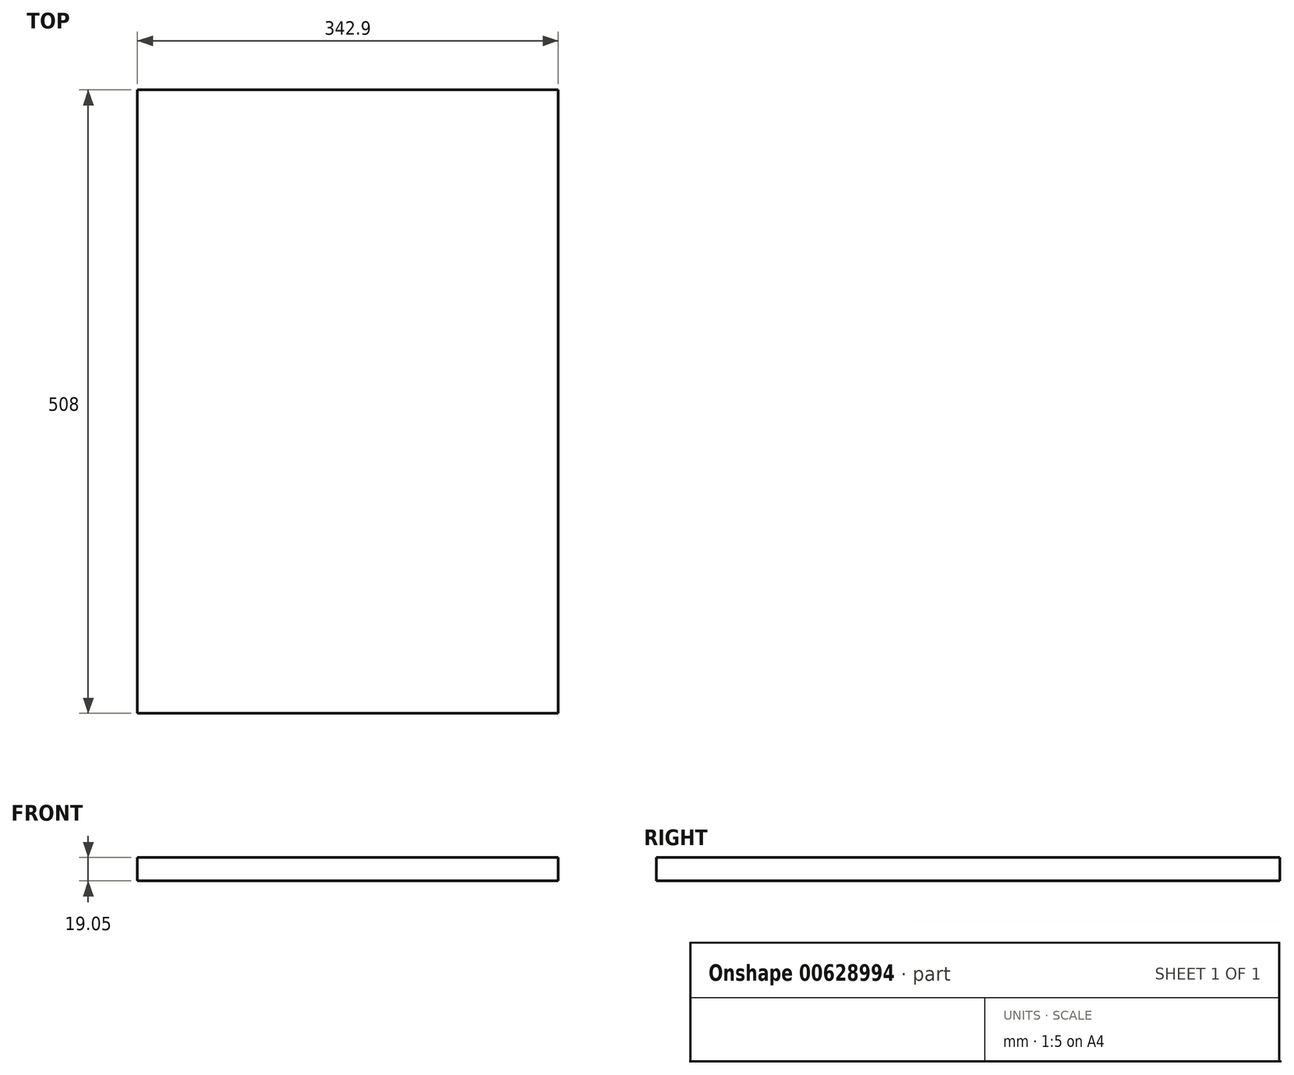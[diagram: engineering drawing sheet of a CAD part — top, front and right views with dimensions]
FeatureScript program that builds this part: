
annotation { "Feature Type Name" : "Feature", "Feature Type Description" : "" }
export const myFeature = defineFeature(function(context is Context, id is Id, definition is map)
    precondition{}
    {
        {
            var Q0;
            Q0=qCreatedBy(makeId("Top.planeOp"),FACE);
            var sketch = newSketch(context, id + "F0", { "sketchPlane" : qUnion([Q0])});
            skLineSegment(sketch, "E0.bottom", {"start": v(-171.45, 254) * mm, "end": v(171.45, 254) * mm});
            skLineSegment(sketch, "E0.top", {"start": v(-171.45, -254) * mm, "end": v(171.45, -254) * mm});
            skLineSegment(sketch, "E0.left", {"start": v(-171.45, 254) * mm, "end": v(-171.45, -254) * mm});
            skLineSegment(sketch, "E0.right", {"start": v(171.45, 254) * mm, "end": v(171.45, -254) * mm});
            skPoint(sketch, "E0.middle", {"position": v(0, 0) * mm});
            skSolve(sketch);
        }
        {
            var Q0;
            Q0=makeQuery(id+"F0.imprint","IMPRINT",FACE,{"disambiguationData":[TD([[makeQuery(id+"F0.imprint","IMPRINT",EDGE,{"derivedFrom":sQuery(id+"F0.wireOp",EDGE,"E0.bottom")}),-1.0]])]});
            extrude(context, id + "F1", {"entities" : qUnion([Q0]), "depth" : 19.05 * mm, "offsetDistance" : 25.4 * mm});
        }
    });
